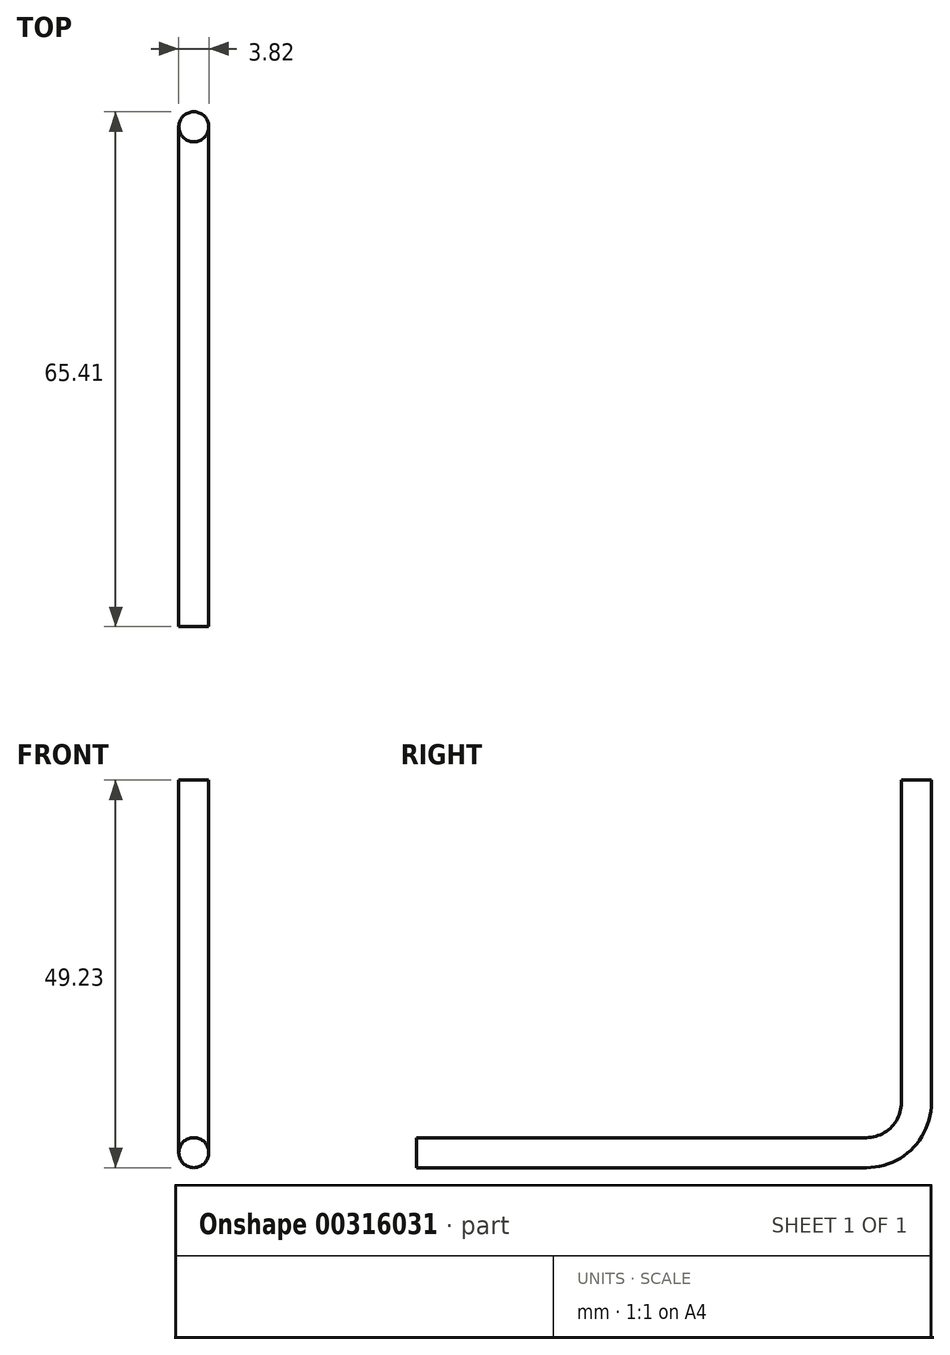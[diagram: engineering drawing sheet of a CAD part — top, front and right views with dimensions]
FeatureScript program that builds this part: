
annotation { "Feature Type Name" : "Feature", "Feature Type Description" : "" }
export const myFeature = defineFeature(function(context is Context, id is Id, definition is map)
    precondition{}
    {
        {
            var Q0;
            Q0=qCreatedBy(makeId("Front.planeOp"),FACE);
            var sketch = newSketch(context, id + "F0", { "sketchPlane" : qUnion([Q0])});
            skCircle(sketch, "E0", {"center": v(0, 0) * mm, "radius": 1.9 * mm});
            skSolve(sketch);
        }
        {
            var Q0;
            Q0=qCreatedBy(makeId("Right.planeOp"),FACE);
            var sketch = newSketch(context, id + "F1", { "sketchPlane" : qUnion([Q0])});
            skLineSegment(sketch, "E1", {"start": v(0, 0) * mm, "end": v(57.15, 0) * mm});
            skArc(sketch, "E2", {"start": v(57.15, 0) * mm, "mid": v(61.64, 1.86) * mm, "end": v(63.5, 6.35) * mm});
            skLineSegment(sketch, "E3", {"start": v(63.5, 6.35) * mm, "end": v(63.5, 47.32) * mm});
            skSolve(sketch);
        }
        {
            var Q0;
            Q0=makeQuery(id+"F0.imprint","IMPRINT",FACE,{"disambiguationData":[TD([[makeQuery(id+"F0.imprint","IMPRINT",EDGE,{"derivedFrom":sQuery(id+"F0.wireOp",EDGE,"E0")}),1.0]])]});
            var Q1;
            Q1=sQuery(id+"F1.wireOp",EDGE,"E1");
            var Q2;
            Q2=sQuery(id+"F1.wireOp",EDGE,"E2");
            var Q3;
            Q3=sQuery(id+"F1.wireOp",EDGE,"E3");
            sweep(context, id + "F2", {"profiles" : qUnion([Q0]), "path" : qUnion([Q1, Q2, Q3])});
        }
    });
